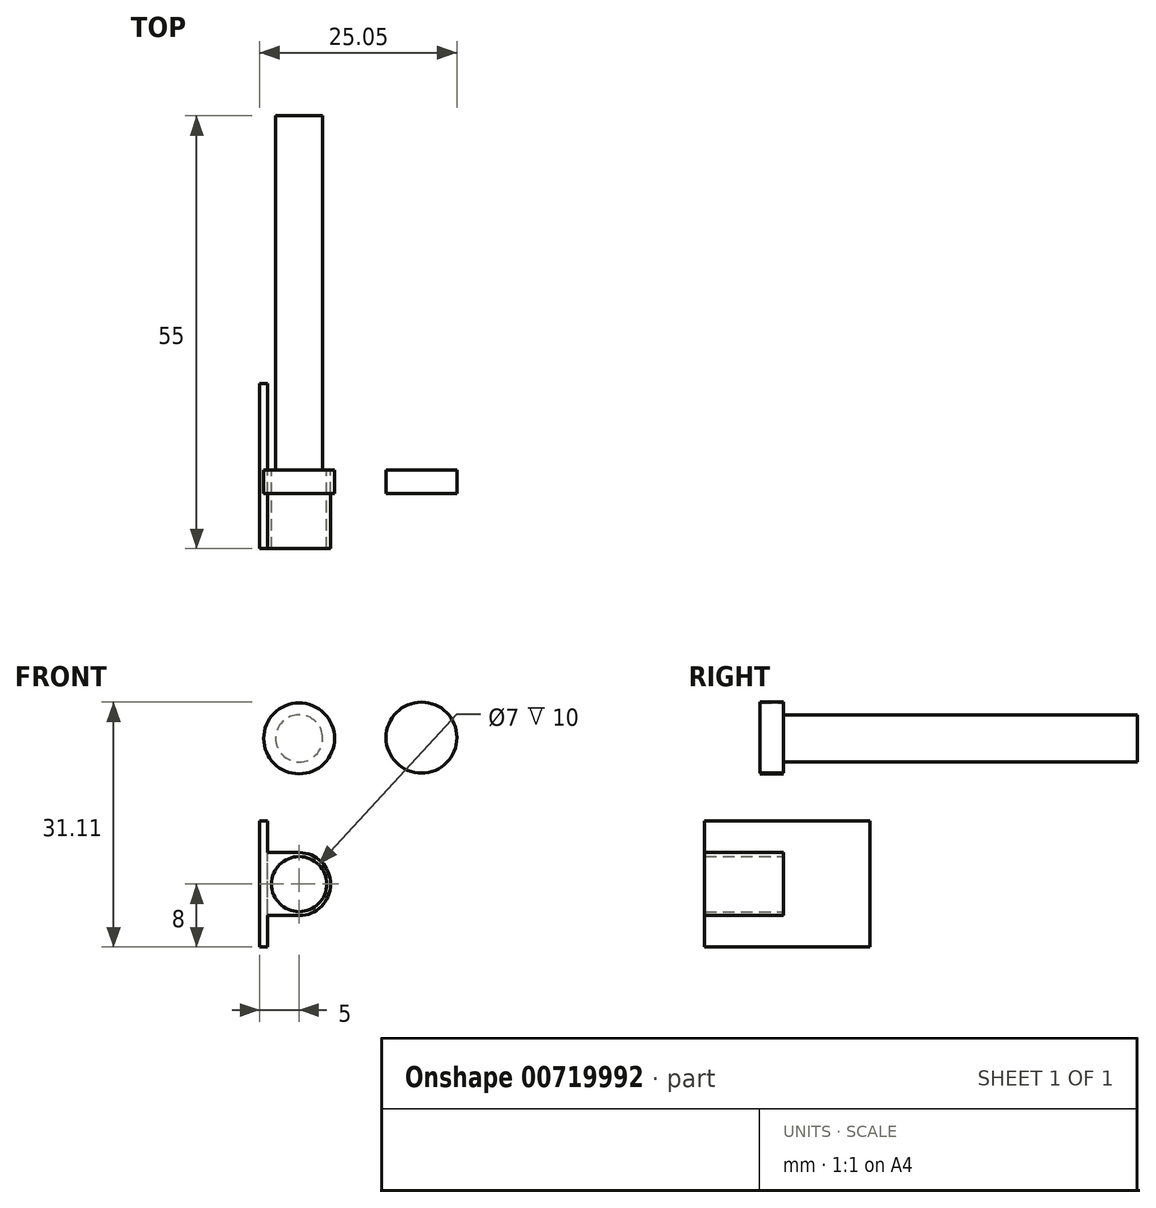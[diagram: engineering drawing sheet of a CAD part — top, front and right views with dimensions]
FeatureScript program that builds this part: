
annotation { "Feature Type Name" : "Feature", "Feature Type Description" : "" }
export const myFeature = defineFeature(function(context is Context, id is Id, definition is map)
    precondition{}
    {
        {
            var Q0;
            Q0=qCreatedBy(makeId("Front.planeOp"),FACE);
            var sketch = newSketch(context, id + "F0", { "sketchPlane" : qUnion([Q0])});
            skCircle(sketch, "E0", {"center": v(0, 0) * mm, "radius": 4 * mm});
            skLineSegment(sketch, "E1.bottom", {"start": v(-4, 0) * mm, "end": v(-5, 0) * mm});
            skLineSegment(sketch, "E1.top", {"start": v(-4, 8) * mm, "end": v(-5, 8) * mm});
            skLineSegment(sketch, "E1.left", {"start": v(-4, 0) * mm, "end": v(-4, 8) * mm});
            skLineSegment(sketch, "E1.right", {"start": v(-5, 0) * mm, "end": v(-5, 8) * mm});
            skLineSegment(sketch, "E2.top", {"start": v(-4, -8) * mm, "end": v(-5, -8) * mm});
            skLineSegment(sketch, "E2.left", {"start": v(-4, 0) * mm, "end": v(-4, -8) * mm});
            skLineSegment(sketch, "E2.right", {"start": v(-5, 0) * mm, "end": v(-5, -8) * mm});
            skCircle(sketch, "E3", {"center": v(0, 0) * mm, "radius": 3.5 * mm});
            skLineSegment(sketch, "E4", {"start": v(0, 4) * mm, "end": v(-4, 4) * mm});
            skLineSegment(sketch, "E5", {"start": v(0, -4) * mm, "end": v(-4, -4) * mm});
            skSolve(sketch);
        }
        {
            var Q0;
            Q0 = qSketchRegion(id + "F0", true);
            extrude(context, id + "F1", {"entities" : qUnion([Q0]), "depth" : 10 * mm, "offsetDistance" : 25 * mm});
        }
        {
            var Q0;
            {var subQ1=sQuery(id+"F0.wireOp",EDGE,"E1.top");Q0=makeQuery(id+"F0.imprint","IMPRINT",FACE,{"disambiguationData":[TD([[makeQuery(id+"F0.imprint","IMPRINT",EDGE,{"derivedFrom":subQ1}),1.0]])]});}
            var Q1;
            {var subQ3=sQuery(id+"F0.wireOp",EDGE,"E1.bottom");Q1=makeQuery(id+"F0.imprint","IMPRINT",FACE,{"disambiguationData":[TD([[makeQuery(id+"F0.imprint","IMPRINT",EDGE,{"derivedFrom":subQ3}),1.0]])]});}
            extrude(context, id + "F2", {"entities" : qUnion([Q0, Q1]), "operationType" : NewBodyOperationType.ADD, "oppositeDirection" : true, "depth" : 11 * mm, "offsetDistance" : 25 * mm});
        }
        {
            var Q0;
            Q0=qCreatedBy(makeId("Front.planeOp"),FACE);
            var sketch = newSketch(context, id + "F3", { "sketchPlane" : qUnion([Q0])});
            skCircle(sketch, "E6", {"center": v(0, 18.51) * mm, "radius": 3 * mm});
            skCircle(sketch, "E7", {"center": v(0, 18.51) * mm, "radius": 4.5 * mm});
            skCircle(sketch, "E8", {"center": v(15.55, 18.61) * mm, "radius": 4.5 * mm});
            skSolve(sketch);
        }
        {
            var Q0;
            Q0 = qSketchRegion(id + "F3", true);
            var Q1;
            Q1=makeQuery(id+"F3.imprint","IMPRINT",FACE,{"disambiguationData":[TD([[makeQuery(id+"F3.imprint","IMPRINT",EDGE,{"derivedFrom":sQuery(id+"F3.wireOp",EDGE,"E6")}),1.0]])]});
            extrude(context, id + "F4", {"entities" : qUnion([Q0, Q1]), "depth" : 3 * mm, "offsetDistance" : 25 * mm});
        }
        {
            var Q0;
            Q0=makeQuery(id+"F3.imprint","IMPRINT",FACE,{"disambiguationData":[TD([[makeQuery(id+"F3.imprint","IMPRINT",EDGE,{"derivedFrom":sQuery(id+"F3.wireOp",EDGE,"E6")}),1.0]])]});
            extrude(context, id + "F5", {"entities" : qUnion([Q0]), "operationType" : NewBodyOperationType.ADD, "oppositeDirection" : true, "depth" : 45 * mm, "offsetDistance" : 25 * mm});
        }
    });
